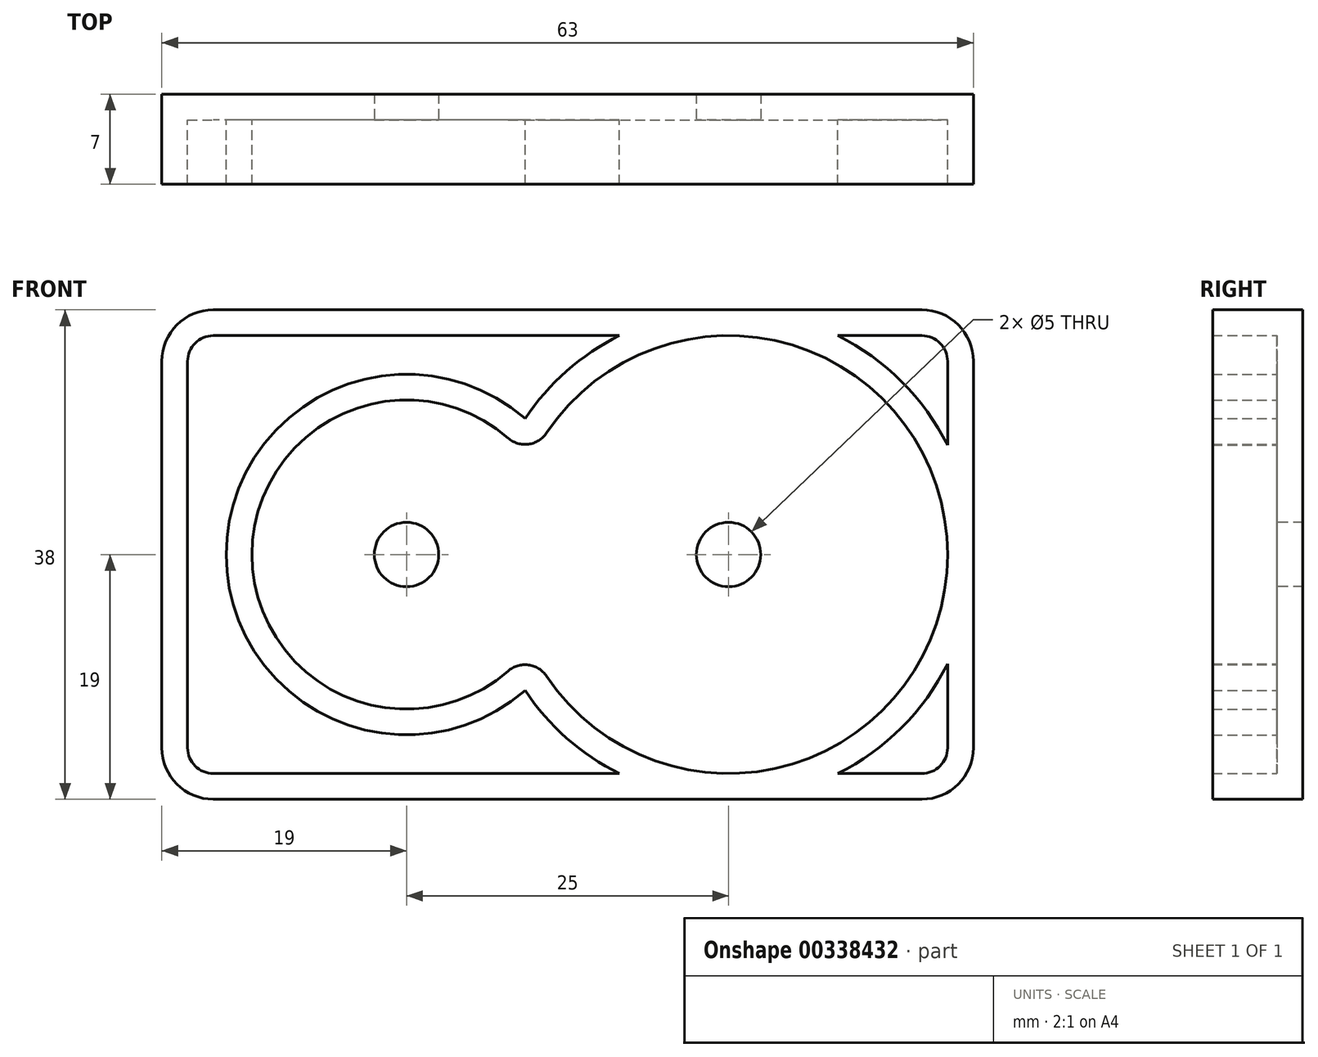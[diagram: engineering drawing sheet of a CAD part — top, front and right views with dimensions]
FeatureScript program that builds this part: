
annotation { "Feature Type Name" : "Feature", "Feature Type Description" : "" }
export const myFeature = defineFeature(function(context is Context, id is Id, definition is map)
    precondition{}
    {
        {
            var Q0;
            Q0=qCreatedBy(makeId("Front.planeOp"),FACE);
            var sketch = newSketch(context, id + "F0", { "sketchPlane" : qUnion([Q0])});
            skLineSegment(sketch, "E0.bottom", {"start": v(27.5, 19) * mm, "end": v(-27.5, 19) * mm});
            skLineSegment(sketch, "E0.top", {"start": v(27.5, -19) * mm, "end": v(-27.5, -19) * mm});
            skLineSegment(sketch, "E0.left", {"start": v(31.5, 15) * mm, "end": v(31.5, -15) * mm});
            skLineSegment(sketch, "E0.right", {"start": v(-31.5, 15) * mm, "end": v(-31.5, -15) * mm});
            skPoint(sketch, "E0.middle", {"position": v(0, 0) * mm});
            skLineSegment(sketch, "E1", {"start": v(-31.5, 0) * mm, "end": v(31.5, 0) * mm, "construction": true});
            skPoint(sketch, "E2", {"position": v(-12.5, 0) * mm});
            skPoint(sketch, "E3", {"position": v(12.5, 0) * mm});
            skLineSegment(sketch, "E4", {"start": v(0, 19) * mm, "end": v(0, -19) * mm, "construction": true});
            skArc(sketch, "E5", {"start": v(-1.64, -9.44) * mm, "mid": v(29.5, 0) * mm, "end": v(-1.64, 9.44) * mm});
            skArc(sketch, "E6", {"start": v(-4.61, 9.05) * mm, "mid": v(-24.5, 0) * mm, "end": v(-4.61, -9.05) * mm});
            skPoint(sketch, "E7.visualSharp", {"position": v(-2.9, 7.2) * mm});
            skArc(sketch, "E7.filletArc", {"start": v(-4.61, 9.05) * mm, "mid": v(-3.04, 8.57) * mm, "end": v(-1.64, 9.44) * mm});
            skPoint(sketch, "E8.visualSharp", {"position": v(-2.9, -7.2) * mm});
            skArc(sketch, "E8.filletArc", {"start": v(-1.64, -9.44) * mm, "mid": v(-3.04, -8.57) * mm, "end": v(-4.61, -9.05) * mm});
            skPoint(sketch, "E9.visualSharp", {"position": v(-31.5, 19) * mm});
            skArc(sketch, "E9.filletArc", {"start": v(-27.5, 19) * mm, "mid": v(-30.33, 17.83) * mm, "end": v(-31.5, 15) * mm});
            skPoint(sketch, "E10.visualSharp", {"position": v(-31.5, -19) * mm});
            skArc(sketch, "E10.filletArc", {"start": v(-31.5, -15) * mm, "mid": v(-30.33, -17.83) * mm, "end": v(-27.5, -19) * mm});
            skPoint(sketch, "E11.visualSharp", {"position": v(31.5, -19) * mm});
            skArc(sketch, "E11.filletArc", {"start": v(27.5, -19) * mm, "mid": v(30.33, -17.83) * mm, "end": v(31.5, -15) * mm});
            skPoint(sketch, "E12.visualSharp", {"position": v(31.5, 19) * mm});
            skArc(sketch, "E12.filletArc", {"start": v(31.5, 15) * mm, "mid": v(30.33, 17.83) * mm, "end": v(27.5, 19) * mm});
            skSolve(sketch);
        }
        {
            var Q0;
            Q0 = qSketchRegion(id + "F0", true);
            extrude(context, id + "F1", {"entities" : qUnion([Q0]), "depth" : 5 * mm});
        }
        {
            var Q0;
            Q0=makeQuery(id+"F1.opExtrude","CAP_FACE",FACE,{"disambiguationData":[OSD([sQuery(id+"F0.wireOp",EDGE,"E0.bottom"),sQuery(id+"F0.wireOp",EDGE,"E0.top"),sQuery(id+"F0.wireOp",EDGE,"E0.left"),sQuery(id+"F0.wireOp",EDGE,"E0.right"),sQuery(id+"F0.wireOp",EDGE,"E5"),sQuery(id+"F0.wireOp",EDGE,"E6"),sQuery(id+"F0.wireOp",EDGE,"E7.filletArc"),sQuery(id+"F0.wireOp",EDGE,"E8.filletArc"),sQuery(id+"F0.wireOp",EDGE,"E9.filletArc"),sQuery(id+"F0.wireOp",EDGE,"E10.filletArc"),sQuery(id+"F0.wireOp",EDGE,"E11.filletArc"),sQuery(id+"F0.wireOp",EDGE,"E12.filletArc")])],"isStart":true});
            var sketch = newSketch(context, id + "F2", { "sketchPlane" : qUnion([Q0])});
            skLineSegment(sketch, "E13.bottom", {"start": v(-27.5, 19) * mm, "end": v(27.5, 19) * mm});
            skLineSegment(sketch, "E13.top", {"start": v(-27.5, -19) * mm, "end": v(27.5, -19) * mm});
            skLineSegment(sketch, "E13.left", {"start": v(-31.5, 15) * mm, "end": v(-31.5, -15) * mm});
            skLineSegment(sketch, "E13.right", {"start": v(31.5, 15) * mm, "end": v(31.5, -15) * mm});
            skPoint(sketch, "E13.middle", {"position": v(0, 0) * mm});
            skPoint(sketch, "E14.visualSharp", {"position": v(31.5, -19) * mm});
            skArc(sketch, "E14.filletArc", {"start": v(27.5, -19) * mm, "mid": v(30.33, -17.83) * mm, "end": v(31.5, -15) * mm});
            skPoint(sketch, "E15.visualSharp", {"position": v(-31.5, -19) * mm});
            skArc(sketch, "E15.filletArc", {"start": v(-31.5, -15) * mm, "mid": v(-30.33, -17.83) * mm, "end": v(-27.5, -19) * mm});
            skPoint(sketch, "E16.visualSharp", {"position": v(-31.5, 19) * mm});
            skArc(sketch, "E16.filletArc", {"start": v(-27.5, 19) * mm, "mid": v(-30.33, 17.83) * mm, "end": v(-31.5, 15) * mm});
            skPoint(sketch, "E17.visualSharp", {"position": v(31.5, 19) * mm});
            skArc(sketch, "E17.filletArc", {"start": v(31.5, 15) * mm, "mid": v(30.33, 17.83) * mm, "end": v(27.5, 19) * mm});
            skSolve(sketch);
        }
        {
            var Q0;
            Q0 = qSketchRegion(id + "F2", true);
            extrude(context, id + "F3", {"entities" : qUnion([Q0]), "operationType" : NewBodyOperationType.ADD, "depth" : 2 * mm});
        }
        {
            var Q0;
            Q0=makeQuery(id+"F1.opExtrude","CAP_FACE",FACE,{"disambiguationData":[OSD([sQuery(id+"F0.wireOp",EDGE,"E0.bottom"),sQuery(id+"F0.wireOp",EDGE,"E0.top"),sQuery(id+"F0.wireOp",EDGE,"E0.left"),sQuery(id+"F0.wireOp",EDGE,"E0.right"),sQuery(id+"F0.wireOp",EDGE,"E5"),sQuery(id+"F0.wireOp",EDGE,"E6"),sQuery(id+"F0.wireOp",EDGE,"E7.filletArc"),sQuery(id+"F0.wireOp",EDGE,"E8.filletArc"),sQuery(id+"F0.wireOp",EDGE,"E9.filletArc"),sQuery(id+"F0.wireOp",EDGE,"E10.filletArc"),sQuery(id+"F0.wireOp",EDGE,"E11.filletArc"),sQuery(id+"F0.wireOp",EDGE,"E12.filletArc")])],"isStart":false});
            shell(context, id + "F4", {"entities" : qUnion([Q0]), "thickness" : 2 * mm});
        }
        {
            var Q0;
            Q0=makeQuery(id+"F3.opExtrude","CAP_FACE",FACE,{"disambiguationData":[OSD([sQuery(id+"F2.wireOp",EDGE,"E13.bottom"),sQuery(id+"F2.wireOp",EDGE,"E13.top"),sQuery(id+"F2.wireOp",EDGE,"E13.left"),sQuery(id+"F2.wireOp",EDGE,"E13.right"),sQuery(id+"F2.wireOp",EDGE,"E14.filletArc"),sQuery(id+"F2.wireOp",EDGE,"E15.filletArc"),sQuery(id+"F2.wireOp",EDGE,"E16.filletArc"),sQuery(id+"F2.wireOp",EDGE,"E17.filletArc")])],"isStart":true});
            var sketch = newSketch(context, id + "F5", { "sketchPlane" : qUnion([Q0])});
            skCircle(sketch, "E18", {"center": v(-12.5, 0) * mm, "radius": 2.5 * mm});
            skCircle(sketch, "E19", {"center": v(12.5, 0) * mm, "radius": 2.5 * mm});
            skSolve(sketch);
        }
        {
            var Q0;
            Q0 = qSketchRegion(id + "F5", true);
            var Q1;
            Q1=makeQuery(id+"F3.opExtrude","CAP_FACE",FACE,{"disambiguationData":[OSD([sQuery(id+"F2.wireOp",EDGE,"E13.bottom"),sQuery(id+"F2.wireOp",EDGE,"E13.top"),sQuery(id+"F2.wireOp",EDGE,"E13.left"),sQuery(id+"F2.wireOp",EDGE,"E13.right"),sQuery(id+"F2.wireOp",EDGE,"E14.filletArc"),sQuery(id+"F2.wireOp",EDGE,"E15.filletArc"),sQuery(id+"F2.wireOp",EDGE,"E16.filletArc"),sQuery(id+"F2.wireOp",EDGE,"E17.filletArc")])],"isStart":false});
            extrude(context, id + "F6", {"entities" : qUnion([Q0]), "operationType" : NewBodyOperationType.REMOVE, "endBound" : BoundingType.UP_TO_SURFACE, "oppositeDirection" : true, "endBoundEntityFace" : qUnion([Q1]), "depth" : 25 * mm});
        }
    });
